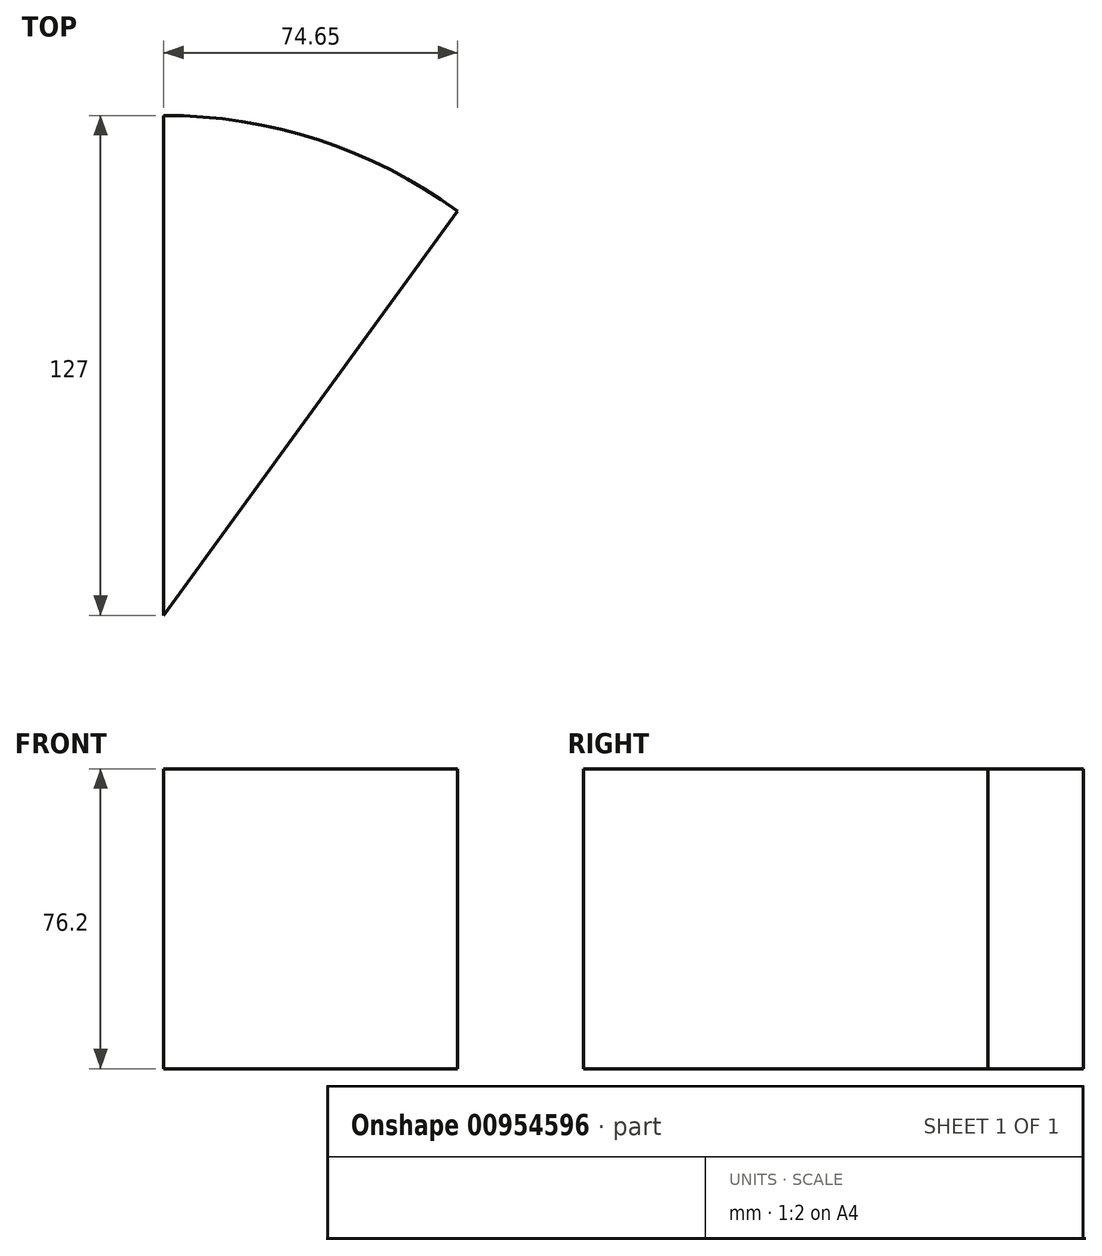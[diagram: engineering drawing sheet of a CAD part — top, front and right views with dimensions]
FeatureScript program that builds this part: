
annotation { "Feature Type Name" : "Feature", "Feature Type Description" : "" }
export const myFeature = defineFeature(function(context is Context, id is Id, definition is map)
    precondition{}
    {
        {
            var Q0;
            Q0=qCreatedBy(makeId("Top.planeOp"),FACE);
            var sketch = newSketch(context, id + "F0", { "sketchPlane" : qUnion([Q0])});
            skCircle(sketch, "E0", {"center": v(0, 0) * mm, "radius": 127 * mm});
            skSolve(sketch);
        }
        {
            var Q0;
            Q0=qCreatedBy(makeId("Top.planeOp"),FACE);
            var sketch = newSketch(context, id + "F1", { "sketchPlane" : qUnion([Q0])});
            skLineSegment(sketch, "E1", {"start": v(0, 0) * mm, "end": v(0, 127) * mm});
            skLineSegment(sketch, "E2", {"start": v(74.65, 102.75) * mm, "end": v(0, 0) * mm});
            skArc(sketch, "E3.0", {"start": v(74.65, 102.75) * mm, "mid": v(39.25, 120.78) * mm, "end": v(0, 127) * mm});
            skSolve(sketch);
        }
        {
            var Q0;
            Q0=makeQuery(id+"F1.imprint","IMPRINT",FACE,{"disambiguationData":[TD([[makeQuery(id+"F1.imprint","IMPRINT",EDGE,{"derivedFrom":sQuery(id+"F1.wireOp",EDGE,"E1")}),-1.0]])]});
            extrude(context, id + "F2", {"entities" : qUnion([Q0]), "depth" : 76.2 * mm, "offsetDistance" : 25.4 * mm});
        }
    });
